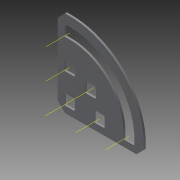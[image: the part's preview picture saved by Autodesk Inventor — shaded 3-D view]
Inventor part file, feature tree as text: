
AUTODESK INVENTOR PART (.ipt)
format: ipt  version: 2015 (Build 190159000, 159)  size: 170,496 bytes
history: native  units: in
note: dims shown in document units (in); Inventor stores cm internally (conversion verified against a paired STEP export)
features: other x10, pattern_linear x2, imported_body x1
ambient origin geometry x8: Origin, YZ Plane, XZ Plane, XY Plane, X Axis, Y Axis, Z Axis, Center Point
bodies: Body1 (feature_tree)
feature tree (13):
  other  "Pivot Gusset"
  parser-record x1  (decoder bookkeeping rows leaked as tree rows — omitted from the tree; the rows remain in map.json)
  other  "main axis"
  pattern_linear  "hoirz axes"  Count1=3 Spacing1=0.5in
  pattern_linear  "vert axes"  Count1=3 Spacing1=0.5in
  other  "diag axis"
  imported_body  "Base1"
  other  "Work Point1"
  other  "Work Axis2"
  other  "Work Axis3"
  other  "Work Axis4"
  other  "Work Axis5"
  other  "Work Point2"
